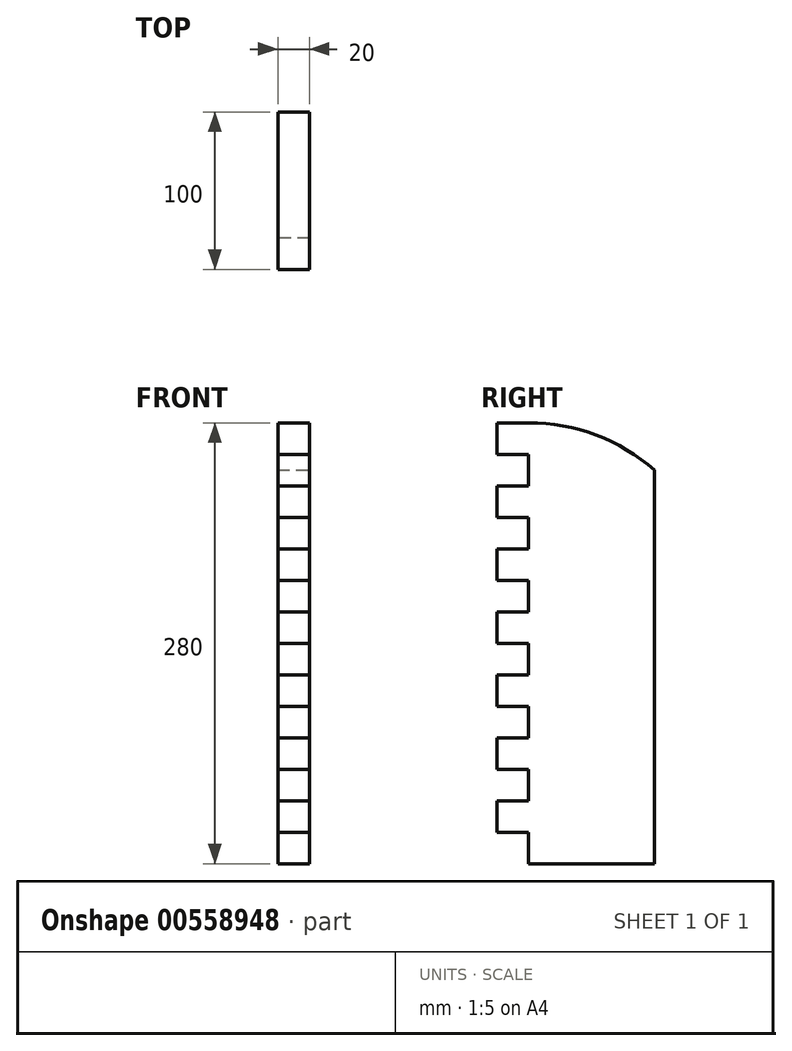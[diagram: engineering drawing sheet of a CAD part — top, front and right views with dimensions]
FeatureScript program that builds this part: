
annotation { "Feature Type Name" : "Feature", "Feature Type Description" : "" }
export const myFeature = defineFeature(function(context is Context, id is Id, definition is map)
    precondition{}
    {
        {
            var Q0;
            Q0=qCreatedBy(makeId("Right.planeOp"),FACE);
            var sketch = newSketch(context, id + "F0", { "sketchPlane" : qUnion([Q0])});
            skLineSegment(sketch, "E0.bottom", {"start": v(50, -140) * mm, "end": v(-50, -140) * mm});
            skLineSegment(sketch, "E0.top", {"start": v(50, 140) * mm, "end": v(-50, 140) * mm});
            skLineSegment(sketch, "E0.left", {"start": v(50, -140) * mm, "end": v(50, 140) * mm});
            skLineSegment(sketch, "E0.right", {"start": v(-50, -140) * mm, "end": v(-50, 140) * mm});
            skPoint(sketch, "E0.middle", {"position": v(0, 0) * mm});
            skSolve(sketch);
        }
        {
            var Q0;
            Q0=makeQuery(id+"F0.imprint","IMPRINT",FACE,{"disambiguationData":[TD([[makeQuery(id+"F0.imprint","IMPRINT",EDGE,{"derivedFrom":sQuery(id+"F0.wireOp",EDGE,"E0.bottom")}),-1.0]])]});
            extrude(context, id + "F1", {"entities" : qUnion([Q0]), "depth" : 20 * mm, "offsetDistance" : 25 * mm});
        }
        {
            var Q0;
            Q0=makeQuery(id+"F1.opExtrude","CAP_FACE",FACE,{"disambiguationData":[OSD([sQuery(id+"F0.wireOp",EDGE,"E0.bottom"),sQuery(id+"F0.wireOp",EDGE,"E0.top"),sQuery(id+"F0.wireOp",EDGE,"E0.left"),sQuery(id+"F0.wireOp",EDGE,"E0.right")])],"isStart":false});
            var sketch = newSketch(context, id + "F2", { "sketchPlane" : qUnion([Q0])});
            skLineSegment(sketch, "E1", {"start": v(50, 110) * mm, "end": v(50, 140) * mm});
            skLineSegment(sketch, "E2", {"start": v(50, 140) * mm, "end": v(-30, 140) * mm});
            skArc(sketch, "E3", {"start": v(50, 110) * mm, "mid": v(12.72, 132.25) * mm, "end": v(-30, 140) * mm});
            skSolve(sketch);
        }
        {
            var Q0;
            Q0=makeQuery(id+"F2.imprint","IMPRINT",FACE,{"disambiguationData":[TD([[makeQuery(id+"F2.imprint","IMPRINT",EDGE,{"derivedFrom":sQuery(id+"F2.wireOp",EDGE,"4YRDexbU-s1fV-oHlm-TiA1-7j8lJWbQxXkN")}),1.0]])]});
            var Q1;
            Q1=makeQuery(id+"F2.imprint","IMPRINT",FACE,{"disambiguationData":[TD([[makeQuery(id+"F2.imprint","IMPRINT",EDGE,{"derivedFrom":sQuery(id+"F2.wireOp",EDGE,"E1")}),1.0]])]});
            extrude(context, id + "F3", {"entities" : qUnion([Q0, Q1]), "operationType" : NewBodyOperationType.REMOVE, "endBound" : BoundingType.UP_TO_NEXT, "oppositeDirection" : true, "depth" : 25 * mm, "offsetDistance" : 25 * mm});
        }
        {
            var Q0;
            Q0=makeQuery(id+"F1.opExtrude","CAP_FACE",FACE,{"disambiguationData":[OSD([sQuery(id+"F0.wireOp",EDGE,"E0.bottom"),sQuery(id+"F0.wireOp",EDGE,"E0.top"),sQuery(id+"F0.wireOp",EDGE,"E0.left"),sQuery(id+"F0.wireOp",EDGE,"E0.right")])],"isStart":true});
            var sketch = newSketch(context, id + "F4", { "sketchPlane" : qUnion([Q0])});
            skLineSegment(sketch, "E4.bottom", {"start": v(50, -140) * mm, "end": v(30, -140) * mm});
            skLineSegment(sketch, "E4.top", {"start": v(50, -120) * mm, "end": v(30, -120) * mm});
            skLineSegment(sketch, "E4.left", {"start": v(50, -140) * mm, "end": v(50, -120) * mm});
            skLineSegment(sketch, "E4.right", {"start": v(30, -140) * mm, "end": v(30, -120) * mm});
            skLineSegment(sketch, "E5.0.1.0", {"start": v(50, -100) * mm, "end": v(30, -100) * mm});
            skLineSegment(sketch, "E5.0.1.1", {"start": v(50, -80) * mm, "end": v(30, -80) * mm});
            skLineSegment(sketch, "E5.0.1.2", {"start": v(50, -100) * mm, "end": v(50, -80) * mm});
            skLineSegment(sketch, "E5.0.1.3", {"start": v(30, -100) * mm, "end": v(30, -80) * mm});
            skLineSegment(sketch, "E5.0.2.0", {"start": v(50, -60) * mm, "end": v(30, -60) * mm});
            skLineSegment(sketch, "E5.0.2.1", {"start": v(50, -40) * mm, "end": v(30, -40) * mm});
            skLineSegment(sketch, "E5.0.2.2", {"start": v(50, -60) * mm, "end": v(50, -40) * mm});
            skLineSegment(sketch, "E5.0.2.3", {"start": v(30, -60) * mm, "end": v(30, -40) * mm});
            skLineSegment(sketch, "E5.0.3.0", {"start": v(50, -20) * mm, "end": v(30, -20) * mm});
            skLineSegment(sketch, "E5.0.3.1", {"start": v(50, 0) * mm, "end": v(30, 0) * mm});
            skLineSegment(sketch, "E5.0.3.2", {"start": v(50, -20) * mm, "end": v(50, 0) * mm});
            skLineSegment(sketch, "E5.0.3.3", {"start": v(30, -20) * mm, "end": v(30, 0) * mm});
            skLineSegment(sketch, "E5.0.4.0", {"start": v(50, 20) * mm, "end": v(30, 20) * mm});
            skLineSegment(sketch, "E5.0.4.1", {"start": v(50, 40) * mm, "end": v(30, 40) * mm});
            skLineSegment(sketch, "E5.0.4.2", {"start": v(50, 20) * mm, "end": v(50, 40) * mm});
            skLineSegment(sketch, "E5.0.4.3", {"start": v(30, 20) * mm, "end": v(30, 40) * mm});
            skLineSegment(sketch, "E5.0.5.0", {"start": v(50, 60) * mm, "end": v(30, 60) * mm});
            skLineSegment(sketch, "E5.0.5.1", {"start": v(50, 80) * mm, "end": v(30, 80) * mm});
            skLineSegment(sketch, "E5.0.5.2", {"start": v(50, 60) * mm, "end": v(50, 80) * mm});
            skLineSegment(sketch, "E5.0.5.3", {"start": v(30, 60) * mm, "end": v(30, 80) * mm});
            skLineSegment(sketch, "E5.0.6.0", {"start": v(50, 100) * mm, "end": v(30, 100) * mm});
            skLineSegment(sketch, "E5.0.6.1", {"start": v(50, 120) * mm, "end": v(30, 120) * mm});
            skLineSegment(sketch, "E5.0.6.2", {"start": v(50, 100) * mm, "end": v(50, 120) * mm});
            skLineSegment(sketch, "E5.0.6.3", {"start": v(30, 100) * mm, "end": v(30, 120) * mm});
            skLineSegment(sketch, "E5.direction1", {"start": v(30, -140) * mm, "end": v(55, -140) * mm, "construction": true});
            skLineSegment(sketch, "E5.direction2", {"start": v(30, -140) * mm, "end": v(30, -100) * mm, "construction": true});
            skSolve(sketch);
        }
        {
            var Q0;
            Q0 = qSketchRegion(id + "F4", true);
            extrude(context, id + "F5", {"entities" : qUnion([Q0]), "operationType" : NewBodyOperationType.REMOVE, "endBound" : BoundingType.UP_TO_NEXT, "oppositeDirection" : true, "depth" : 25 * mm, "offsetDistance" : 25 * mm});
        }
    });
